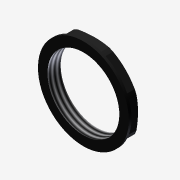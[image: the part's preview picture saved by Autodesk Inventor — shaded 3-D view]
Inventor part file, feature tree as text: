
AUTODESK INVENTOR PART (.ipt)
format: ipt  version: 2016 SP1 (Build 200210100, 210)  size: 108,032 bytes
history: native  units: mm
features: imported_body x1, thread x1
ambient origin geometry x8: Origin, YZ Plane, XZ Plane, XY Plane, X Axis, Y Axis, Z Axis, Center Point
bodies: Solid1 (feature_tree)
feature tree (2):
  imported_body  "Base1"
  thread  "Thread1"  [1 undecoded]
note: 1 required parameter value undecoded (feature->parameter linkage not recoverable at this tier; creation-order binding heuristic only, values carry confidence <= 0.55)
